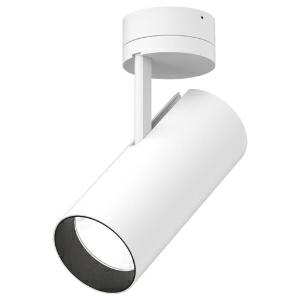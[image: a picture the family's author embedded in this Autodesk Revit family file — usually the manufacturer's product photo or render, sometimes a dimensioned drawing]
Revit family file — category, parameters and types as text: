
# Revit family: imagine_320-0802
name_source: partatom
category: Leuchten
revit_build: Autodesk Revit 2016 (Build: 20190508_0715(x64)
units: mm (PartAtom-declared; Revit-internal decimal feet)

## family parameters
Basisbauteil = Fläche
Beim Laden mit Abzugskörper schneiden = Nein
Bemaßung runder Anschluss = Durchmesser verwenden
Gemeinsam genutzt = Nein
Lichtquelle = Nein
Raumberechnungspunkt = Nein
Teiletyp = Normal

## types (1)
- 320-0802-H27-T00-W22 (1 x LED, 2909.09 lm, 27.6 W, 2700K)
    Beschreibung = IMAGINE
    CIE Flux Codes = 100 100 100 100 70
    Color Rendering = 1A/90…99
    Color Temperature = 2700K
    Height = 260 mm
    Hersteller = Prolicht
    Lamp Light Flux = 2909.09 lm
    Lamp Power = 27.6 W
    Lamp count = 1
    Lampe = 1 x LED
    Length = 90 mm
    Luminous efficacy = 74 lm/W
    ModVariant = Nein
    Modell = 320-0802
    Mounting Place = Ceiling
    Mounting Type = Surface mounted
    Number of Poles = 1
    OnlyDefault = Ja
    Power Factor = 1
    Product Name = IMAGINE
    Product group = Surface spotlights
    ProductGroupID = 332
    Protection Class = Protection class
    Protection Degree = Degree of protection
    RLX_Detail_Level = 1
    RlxData = <blob elided: 103853 chars, md5=591c881a>
    Scheinlast = 28 VA
    Socket = socket
    Standby Power = 0 W
    System Light Flux = 2045 lm
    System Power = 28 W
    Typenbild = 320-0802.jpg
    Typenkommentare = LED COLOUR DIR 2700 K (27),OPTICS ABSICHTLICH_LEER (00),BEAMWIDTH Spot (22)
    URL = http://relux.com
    VarID = 320-0802-h27-t00-w22
    Voltage = 0 V
    Vorgabe-Ansicht = 1800 mm
    Weight = 0.00 kg
    Width = 0 mm  [stored 0 ft]

note: [stored X ft] marks values corroborated as IEEE doubles in the binary element streams (Revit-internal decimal feet)

## geometry (parser evidence)
native form markers: Sweep x13
no freeform markers — native parametric forms only
